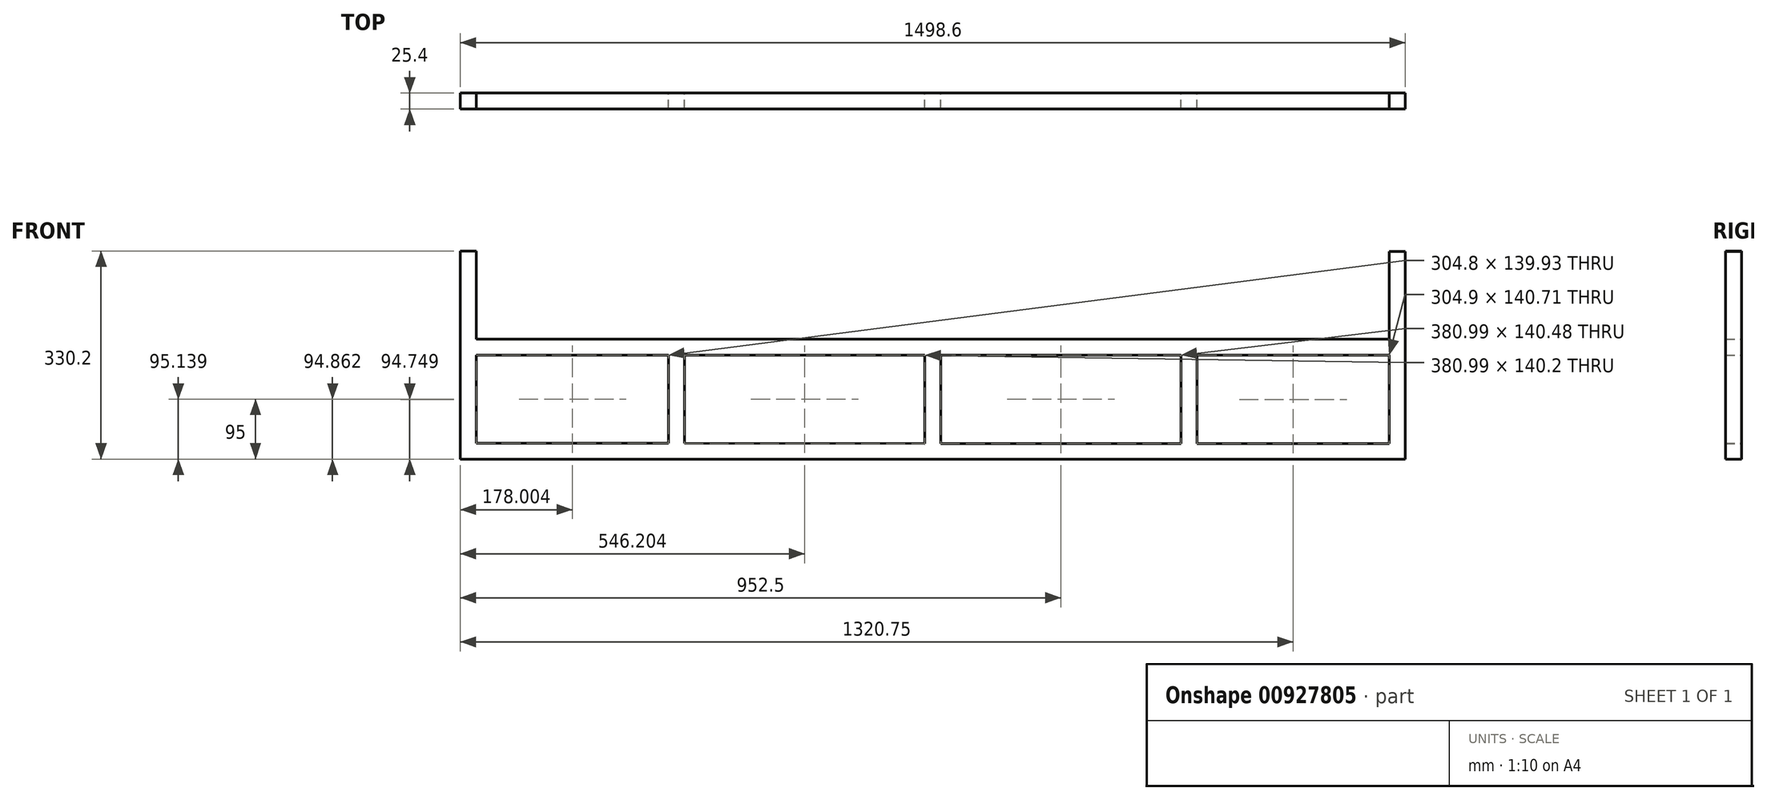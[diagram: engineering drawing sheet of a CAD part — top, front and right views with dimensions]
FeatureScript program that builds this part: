
annotation { "Feature Type Name" : "Feature", "Feature Type Description" : "" }
export const myFeature = defineFeature(function(context is Context, id is Id, definition is map)
    precondition{}
    {
        {
            var Q0;
            Q0=qCreatedBy(makeId("Front.planeOp"),FACE);
            var sketch = newSketch(context, id + "F0", { "sketchPlane" : qUnion([Q0])});
            skLineSegment(sketch, "E0", {"start": v(-342.97, 12.58) * mm, "end": v(1155.63, 12.58) * mm});
            skLineSegment(sketch, "E1", {"start": v(1155.63, 12.58) * mm, "end": v(1155.63, 36.96) * mm});
            skLineSegment(sketch, "E2", {"start": v(-342.97, 12.58) * mm, "end": v(-342.97, 37.98) * mm});
            skLineSegment(sketch, "E3", {"start": v(-342.97, 37.98) * mm, "end": v(1155.63, 36.96) * mm});
            skLineSegment(sketch, "E4", {"start": v(-342.97, 37.98) * mm, "end": v(-342.77, 342.78) * mm});
            skLineSegment(sketch, "E5", {"start": v(-342.77, 342.78) * mm, "end": v(-317.37, 342.78) * mm});
            skLineSegment(sketch, "E6", {"start": v(-317.37, 342.78) * mm, "end": v(-317.37, 12.58) * mm});
            skLineSegment(sketch, "E7", {"start": v(1155.63, 36.96) * mm, "end": v(1155.63, 341.76) * mm});
            skLineSegment(sketch, "E8", {"start": v(1155.63, 341.76) * mm, "end": v(1130.23, 341.76) * mm});
            skLineSegment(sketch, "E9", {"start": v(1130.23, 341.76) * mm, "end": v(1130.23, 36.98) * mm});
            skLineSegment(sketch, "E10.bottom", {"start": v(-317.37, 177.68) * mm, "end": v(1130.23, 177.68) * mm});
            skLineSegment(sketch, "E10.top", {"start": v(-317.37, 203.08) * mm, "end": v(1130.23, 203.08) * mm});
            skLineSegment(sketch, "E10.left", {"start": v(-317.37, 177.68) * mm, "end": v(-317.37, 203.08) * mm});
            skLineSegment(sketch, "E10.right", {"start": v(1130.23, 177.68) * mm, "end": v(1130.23, 203.08) * mm});
            skLineSegment(sketch, "E11", {"start": v(-12.57, 177.68) * mm, "end": v(-12.57, 37.76) * mm});
            skLineSegment(sketch, "E12", {"start": v(-12.57, 37.76) * mm, "end": v(12.74, 37.74) * mm});
            skLineSegment(sketch, "E13", {"start": v(12.74, 37.74) * mm, "end": v(12.83, 177.68) * mm});
            skLineSegment(sketch, "E14", {"start": v(12.83, 177.68) * mm, "end": v(-12.57, 177.68) * mm});
            skLineSegment(sketch, "E15", {"start": v(825.43, 177.68) * mm, "end": v(825.33, 37.18) * mm});
            skLineSegment(sketch, "E16", {"start": v(825.33, 37.18) * mm, "end": v(799.93, 37.2) * mm});
            skLineSegment(sketch, "E17", {"start": v(799.93, 37.2) * mm, "end": v(800.03, 177.68) * mm});
            skLineSegment(sketch, "E18", {"start": v(800.03, 177.68) * mm, "end": v(825.43, 177.68) * mm});
            skLineSegment(sketch, "E19", {"start": v(406.43, 177.68) * mm, "end": v(406.33, 37.47) * mm});
            skLineSegment(sketch, "E20", {"start": v(406.33, 37.47) * mm, "end": v(419.03, 37.46) * mm});
            skLineSegment(sketch, "E21", {"start": v(419.03, 37.46) * mm, "end": v(419.13, 177.68) * mm});
            skLineSegment(sketch, "E22", {"start": v(419.13, 177.68) * mm, "end": v(393.73, 177.68) * mm});
            skLineSegment(sketch, "E23", {"start": v(393.73, 177.68) * mm, "end": v(393.73, 37.48) * mm});
            skSolve(sketch);
        }
        {
            var Q0;
            {var subQ19=sQuery(id+"F0.wireOp",EDGE,"E10.top");var subQ29=sQuery(id+"F0.wireOp",EDGE,"E7");var subQ30=sQuery(id+"F0.wireOp",EDGE,"E1");var subQ42=sQuery(id+"F0.wireOp",EDGE,"E4");var subQ43=sQuery(id+"F0.wireOp",EDGE,"E2");Q0=qUnion([makeQuery(id+"F0.imprint","IMPRINT",FACE,{"disambiguationData":[TD([[makeQuery(id+"F0.imprint","IMPRINT",EDGE,{"derivedFrom":subQ43}),-1.0]])]}),makeQuery(id+"F0.imprint","IMPRINT",FACE,{"disambiguationData":[TD([[makeQuery(id+"F0.imprint","IMPRINT",EDGE,{"derivedFrom":subQ42}),-1.0]])]}),makeQuery(id+"F0.imprint","IMPRINT",FACE,{"disambiguationData":[TD([[makeQuery(id+"F0.imprint","IMPRINT",EDGE,{"derivedFrom":subQ29}),1.0]])]}),makeQuery(id+"F0.imprint","IMPRINT",FACE,{"disambiguationData":[TD([[makeQuery(id+"F0.imprint","IMPRINT",EDGE,{"derivedFrom":subQ30}),1.0]])]}),makeQuery(id+"F0.imprint","IMPRINT",FACE,{"disambiguationData":[TD([[makeQuery(id+"F0.imprint","IMPRINT",EDGE,{"derivedFrom":subQ19}),-1.0]])]})]);}
            var Q1;
            {var subQ2=sQuery(id+"F0.wireOp",EDGE,"E11");Q1=makeQuery(id+"F0.imprint","IMPRINT",FACE,{"disambiguationData":[TD([[makeQuery(id+"F0.imprint","IMPRINT",EDGE,{"derivedFrom":subQ2}),1.0]])]});}
            var Q2;
            {var subQ0=sQuery(id+"F0.wireOp",EDGE,"E19");Q2=makeQuery(id+"F0.imprint","IMPRINT",FACE,{"disambiguationData":[TD([[makeQuery(id+"F0.imprint","IMPRINT",EDGE,{"derivedFrom":subQ0}),1.0]])]});}
            var Q3;
            {var subQ0=sQuery(id+"F0.wireOp",EDGE,"E19");Q3=makeQuery(id+"F0.imprint","IMPRINT",FACE,{"disambiguationData":[TD([[makeQuery(id+"F0.imprint","IMPRINT",EDGE,{"derivedFrom":subQ0}),-1.0]])]});}
            var Q4;
            {var subQ0=sQuery(id+"F0.wireOp",EDGE,"E15");Q4=makeQuery(id+"F0.imprint","IMPRINT",FACE,{"disambiguationData":[TD([[makeQuery(id+"F0.imprint","IMPRINT",EDGE,{"derivedFrom":subQ0}),-1.0]])]});}
            extrude(context, id + "F1", {"entities" : qUnion([Q0, Q1, Q2, Q3, Q4]), "depth" : 25.4 * mm, "offsetDistance" : 25.4 * mm});
        }
    });
